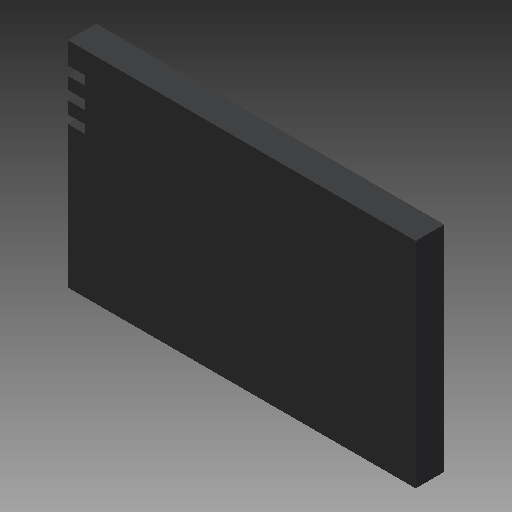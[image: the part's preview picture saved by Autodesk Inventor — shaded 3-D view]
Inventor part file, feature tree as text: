
AUTODESK INVENTOR PART (.ipt)
format: ipt  version: 2017 (Build 210142000, 142)  size: 102,912 bytes
history: native  units: mm
features: extrude x2, sketch x2
ambient origin geometry x8: Origin, YZ Plane, XZ Plane, XY Plane, X Axis, Y Axis, Z Axis, Center Point
bodies: Solid1 (feature_tree)
feature tree (4):
  extrude  "Extrusion1"  Depth=62.2mm
  extrude  "Extrusion2"  Depth=13.0mm
  sketch  "Sketch1"  dims[d0=38.3mm d1=62.2mm]
  sketch  "Sketch2"  dims[d2=5.1mm d3=0.0mm d4=13.0mm d5=3.0mm d6=3.9mm d7=1.6mm d8=2.2mm d9=1.6mm d10=2.2mm d11=3.6mm d12=0.0mm]
